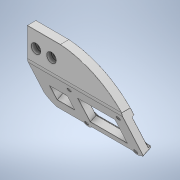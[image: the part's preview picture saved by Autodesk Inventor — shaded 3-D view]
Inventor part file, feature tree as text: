
AUTODESK INVENTOR PART (.ipt)
format: ipt  version: 2021 (Build 250183000, 183)  size: 474,112 bytes
history: native  units: mm
features: extrude x6, sketch x5, projected_geometry x4, revolve x1, fillet x1
ambient origin geometry x8: Origin, YZ Plane, XZ Plane, XY Plane, X Axis, Y Axis, Z Axis, Center Point
bodies: Solid1 (feature_tree)
feature tree (17):
  sketch  "Sketch1"  dims[d0=4.3mm d1=4.3mm d2=11.6mm d3=8.05mm d4=11.6mm d5=8.5mm d6=8.5mm d7=86.23mm d8=8.0mm d9=0.0mm]
  extrude  "Extrusion1"  Depth=8.0mm TaperAngle=0.0deg
  extrude  "Extrusion2"  Depth=4.0mm
  revolve  "Revolution1"  [1 undecoded]
  extrude  "Extrusion3"  Depth=6.6mm
  sketch  "Sketch5"  dims[d37=6.6mm d38=6.6mm]
  extrude  "Extrusion4"  Depth=0.2mm
  extrude  "Extrusion5"  Depth=0.2mm
  extrude  "Extrusion6"  Depth=0.2mm
  fillet  "Fillet1"  Radius=3.2mm
  sketch  "Sketch2"  dims[d10=4.0mm d11=0.0mm d12=4.363323mm]
  projected_geometry  "Projected Loop1"
  sketch  "Sketch3"  dims[d13=49.0mm d14=0.0mm d36=3.2mm]
  projected_geometry  "Projected Loop2"
  projected_geometry  "Projected Loop4"
  sketch  "Sketch6"  dims[d39=3.2mm d40=48.0mm d41=3.2mm d42=41.0mm d43=3.2mm d44=33.8mm d45=26.8mm d46=5.5mm d47=5.5mm d48=16.0mm d49=16.0mm d50=12.182mm d51=11.523mm d52=8.0mm d53=8.0mm d54=8.0mm d55=8.0mm d56=0.0mm d57=0.0mm d58=2.0mm d59=0.0mm d60=30.23mm d61=0.0mm d62=0.0mm d63=0.2mm d64=0.2mm d65=0.2mm d66=0.872665mm d67=0.872665mm]
  projected_geometry  "Projected Loop5"
note: 1 required parameter value undecoded (feature->parameter linkage not recoverable at this tier; creation-order binding heuristic only, values carry confidence <= 0.55)
